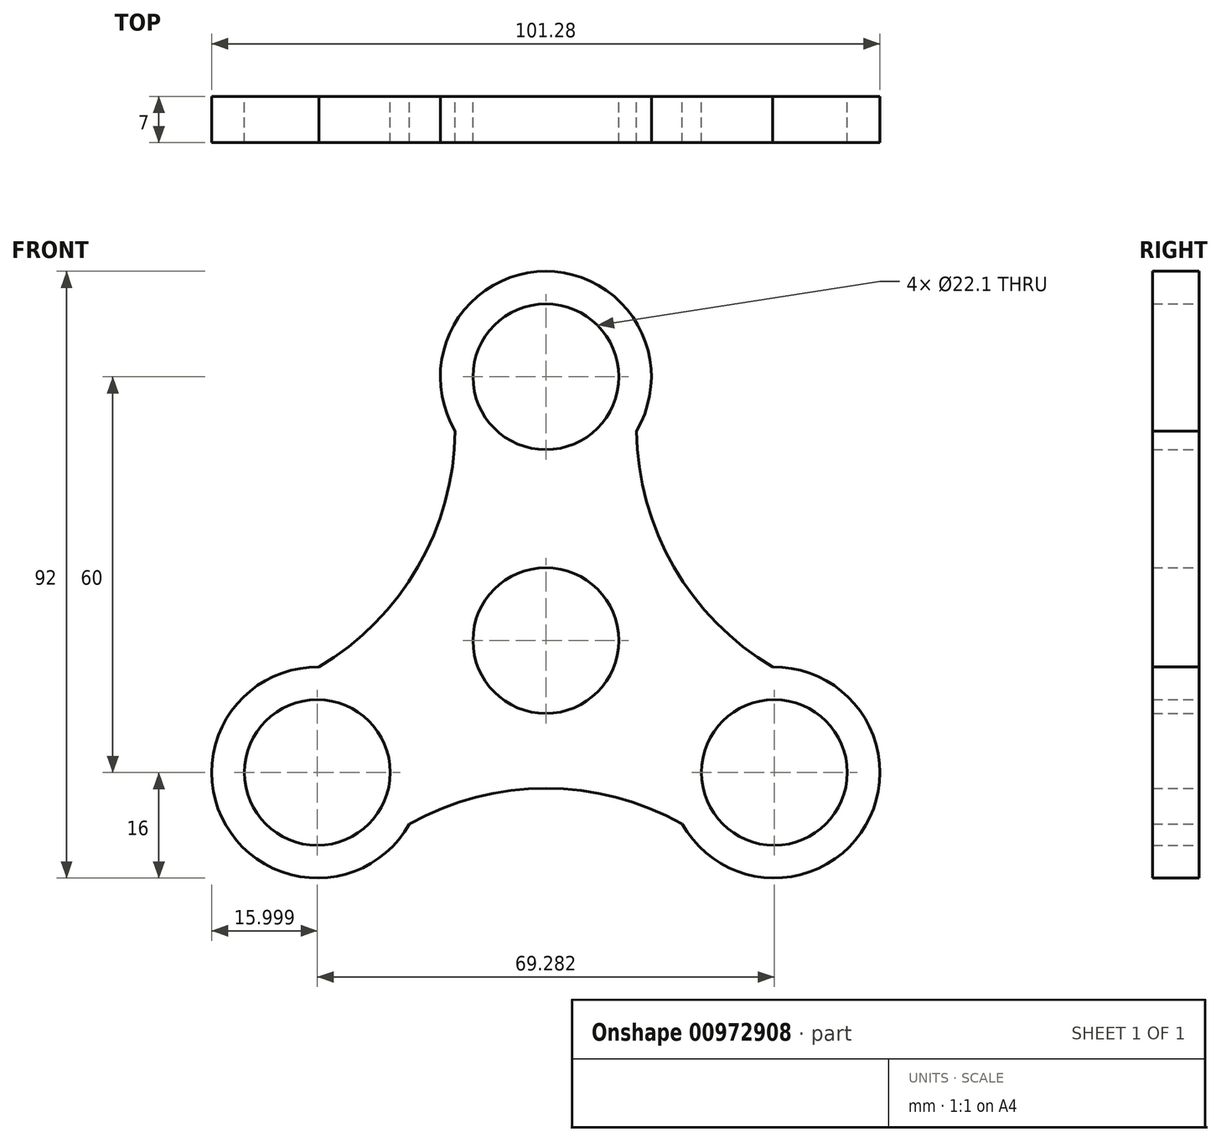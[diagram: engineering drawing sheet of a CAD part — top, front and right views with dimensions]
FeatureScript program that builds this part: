
annotation { "Feature Type Name" : "Feature", "Feature Type Description" : "" }
export const myFeature = defineFeature(function(context is Context, id is Id, definition is map)
    precondition{}
    {
        {
            var Q0;
            Q0=qCreatedBy(makeId("Front.planeOp"),FACE);
            var sketch = newSketch(context, id + "F0", { "sketchPlane" : qUnion([Q0])});
            skCircle(sketch, "E0", {"center": v(0, 0) * mm, "radius": 11.05 * mm});
            skCircle(sketch, "E1", {"center": v(0, 40) * mm, "radius": 11.05 * mm});
            skCircle(sketch, "E2.1.0", {"center": v(-34.64, -20) * mm, "radius": 11.05 * mm});
            skCircle(sketch, "E2.2.0", {"center": v(34.64, -20) * mm, "radius": 11.05 * mm});
            skCircle(sketch, "E3", {"center": v(0, 40) * mm, "radius": 16 * mm});
            skCircle(sketch, "E4.1.0", {"center": v(-34.64, -20) * mm, "radius": 16 * mm});
            skCircle(sketch, "E4.2.0", {"center": v(34.64, -20) * mm, "radius": 16 * mm});
            skLineSegment(sketch, "E5", {"start": v(0, 40) * mm, "end": v(34.64, -20) * mm, "construction": true});
            skLineSegment(sketch, "E6", {"start": v(9.34, 39.4) * mm, "end": v(34.64, -4.42) * mm, "construction": true});
            skArc(sketch, "E7", {"start": v(13.74, 31.8) * mm, "mid": v(19.4, 11.2) * mm, "end": v(34.4, -4) * mm});
            skArc(sketch, "E8.1.0", {"start": v(-34.4, -4) * mm, "mid": v(-19.4, 11.2) * mm, "end": v(-13.74, 31.8) * mm});
            skArc(sketch, "E8.2.0", {"start": v(20.67, -27.8) * mm, "mid": v(0, -22.4) * mm, "end": v(-20.67, -27.8) * mm});
            skSolve(sketch);
        }
        {
            var Q0;
            Q0=makeQuery(id+"F0.imprint","IMPRINT",FACE,{"disambiguationData":[TD([[makeQuery(id+"F0.imprint","IMPRINT",EDGE,{"derivedFrom":sQuery(id+"F0.wireOp",EDGE,"E2.1.0")}),-1.0]])]});
            var Q1;
            Q1=makeQuery(id+"F0.imprint","IMPRINT",FACE,{"disambiguationData":[TD([[makeQuery(id+"F0.imprint","IMPRINT",EDGE,{"derivedFrom":sQuery(id+"F0.wireOp",EDGE,"E0")}),-1.0]])]});
            var Q2;
            Q2=makeQuery(id+"F0.imprint","IMPRINT",FACE,{"disambiguationData":[TD([[makeQuery(id+"F0.imprint","IMPRINT",EDGE,{"derivedFrom":sQuery(id+"F0.wireOp",EDGE,"E1")}),-1.0]])]});
            var Q3;
            Q3=makeQuery(id+"F0.imprint","IMPRINT",FACE,{"disambiguationData":[TD([[makeQuery(id+"F0.imprint","IMPRINT",EDGE,{"derivedFrom":sQuery(id+"F0.wireOp",EDGE,"E2.2.0")}),-1.0]])]});
            extrude(context, id + "F1", {"entities" : qUnion([Q0, Q1, Q2, Q3]), "depth" : 7 * mm, "offsetDistance" : 25 * mm});
        }
    });
